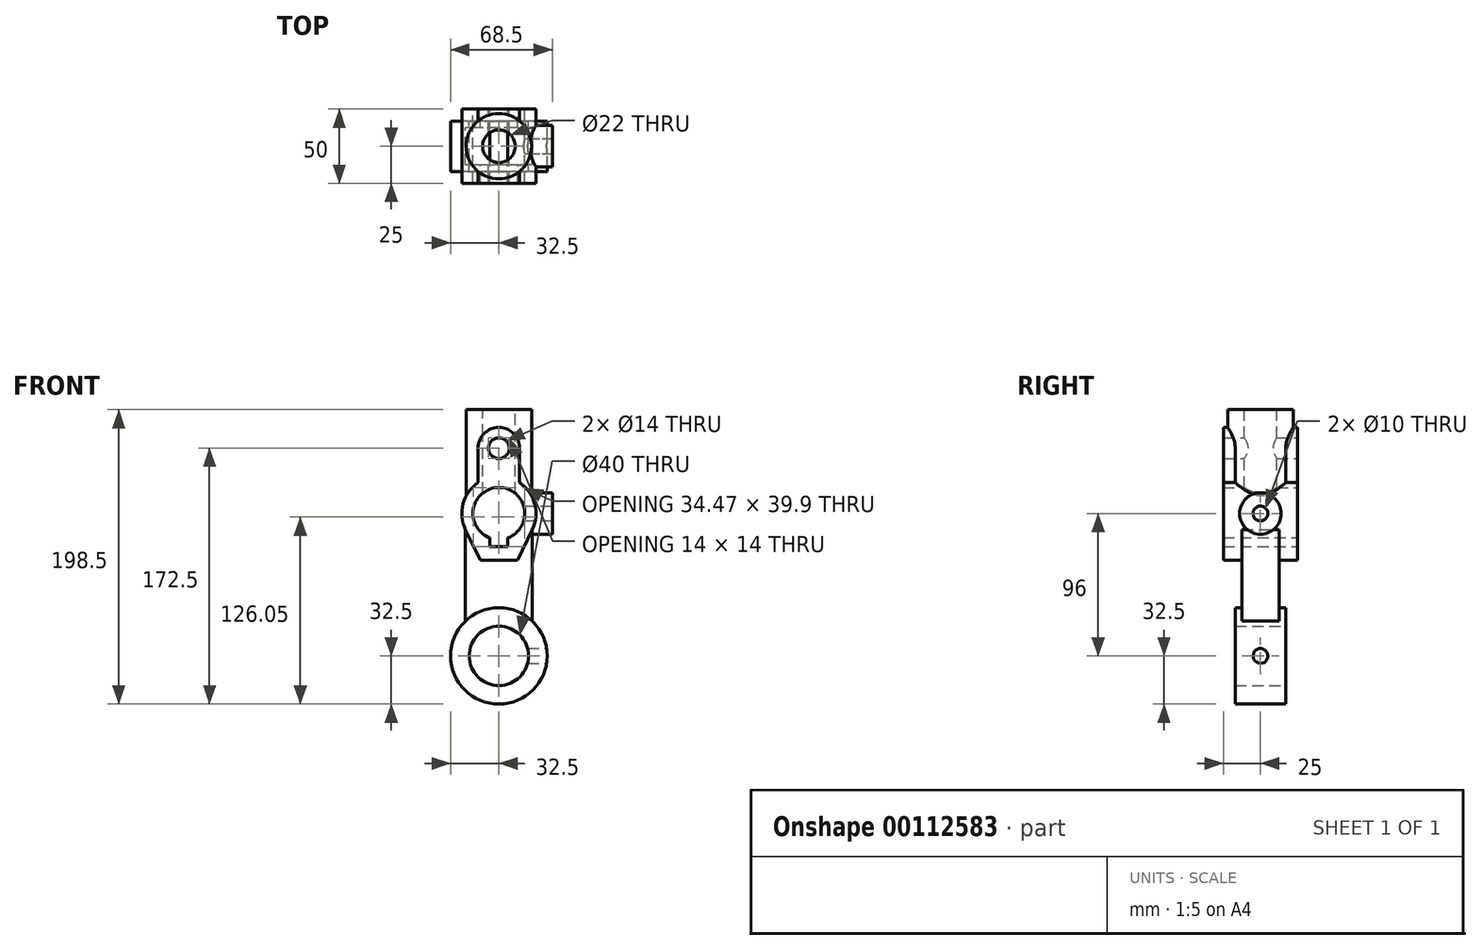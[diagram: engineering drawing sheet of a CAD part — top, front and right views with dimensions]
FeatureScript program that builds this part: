
annotation { "Feature Type Name" : "Feature", "Feature Type Description" : "" }
export const myFeature = defineFeature(function(context is Context, id is Id, definition is map)
    precondition{}
    {
        {
            var Q0;
            Q0=qCreatedBy(makeId("Front.planeOp"),FACE);
            var sketch = newSketch(context, id + "F0", { "sketchPlane" : qUnion([Q0])});
            skCircle(sketch, "E0", {"center": v(0, 0) * mm, "radius": 32.5 * mm});
            skCircle(sketch, "E1", {"center": v(0, 0) * mm, "radius": 20 * mm});
            skSolve(sketch);
        }
        {
            var Q0;
            Q0 = qSketchRegion(id + "F0", true);
            extrude(context, id + "F1", {"entities" : qUnion([Q0]), "depth" : 34 * mm, "symmetric" : true});
        }
        {
            var Q0;
            Q0=qCreatedBy(makeId("Front.planeOp"),FACE);
            var sketch = newSketch(context, id + "F2", { "sketchPlane" : qUnion([Q0])});
            skLineSegment(sketch, "E2.bottom", {"start": v(-22.5, 0) * mm, "end": v(22.5, 0) * mm});
            skLineSegment(sketch, "E2.top", {"start": v(-22.5, 96) * mm, "end": v(22.5, 96) * mm});
            skLineSegment(sketch, "E2.left", {"start": v(-22.5, 0) * mm, "end": v(-22.5, 96) * mm});
            skLineSegment(sketch, "E2.right", {"start": v(22.5, 0) * mm, "end": v(22.5, 96) * mm});
            skLineSegment(sketch, "E3", {"start": v(0, 64.95) * mm, "end": v(-22.5, 64.95) * mm, "construction": true});
            skLineSegment(sketch, "E4", {"start": v(0, 56.14) * mm, "end": v(22.5, 56.14) * mm, "construction": true});
            skSolve(sketch);
        }
        {
            var Q0;
            Q0 = qSketchRegion(id + "F2", true);
            extrude(context, id + "F3", {"entities" : qUnion([Q0]), "operationType" : NewBodyOperationType.ADD, "depth" : 25 * mm, "symmetric" : true});
        }
        {
            var Q0;
            {var subQ0=sQuery(id+"F2.wireOp",EDGE,"E2.bottom");Q0=makeQuery(id+"F3.boolean.opBoolean","SPLIT",FACE,{"disambiguationData":[TD([makeQuery(id+"F1.opExtrude","SWEPT_FACE",FACE,{"disambiguationData":[OSD([sQuery(id+"F0.wireOp",EDGE,"E1")])]})])],"derivedFrom":makeQuery(id+"F3.opExtrude","CAP_FACE",FACE,{"disambiguationData":[OSD([subQ0,sQuery(id+"F2.wireOp",EDGE,"E2.top"),sQuery(id+"F2.wireOp",EDGE,"E2.left"),sQuery(id+"F2.wireOp",EDGE,"E2.right")])],"isStart":false})});}
            extrude(context, id + "F4", {"entities" : qUnion([Q0]), "operationType" : NewBodyOperationType.REMOVE, "endBound" : BoundingType.THROUGH_ALL, "oppositeDirection" : true, "depth" : 25 * mm});
        }
        {
            var Q0;
            Q0=qCreatedBy(makeId("Front.planeOp"),FACE);
            var sketch = newSketch(context, id + "F5", { "sketchPlane" : qUnion([Q0])});
            skCircle(sketch, "E5", {"center": v(0, 140) * mm, "radius": 7 * mm});
            skArc(sketch, "E6", {"start": v(6, 79.56) * mm, "mid": v(0, 113.5) * mm, "end": v(-6, 79.56) * mm});
            skLineSegment(sketch, "E7", {"start": v(-6, 79.56) * mm, "end": v(-6, 73.6) * mm});
            skLineSegment(sketch, "E8", {"start": v(6, 79.56) * mm, "end": v(6, 73.6) * mm});
            skLineSegment(sketch, "E9", {"start": v(6, 73.6) * mm, "end": v(-6, 73.6) * mm});
            skArc(sketch, "E10", {"start": v(-14, 140) * mm, "mid": v(0, 154) * mm, "end": v(14, 140) * mm});
            skLineSegment(sketch, "E11", {"start": v(-14, 140) * mm, "end": v(-14, 116.71) * mm});
            skLineSegment(sketch, "E12", {"start": v(14, 140) * mm, "end": v(14, 116.71) * mm});
            skArc(sketch, "E13", {"start": v(-14, 116.71) * mm, "mid": v(-24.14, 102.5) * mm, "end": v(-22.5, 85.1) * mm});
            skLineSegment(sketch, "E14.0", {"start": v(-22.5, 0) * mm, "end": v(-22.5, 85.1) * mm});
            skLineSegment(sketch, "E15", {"start": v(-22.5, 85.1) * mm, "end": v(-22.5, 96) * mm});
            skLineSegment(sketch, "E16.0", {"start": v(22.5, 0) * mm, "end": v(22.5, 96) * mm});
            skArc(sketch, "E17", {"start": v(22.5, 85.1) * mm, "mid": v(24.14, 102.5) * mm, "end": v(14, 116.71) * mm});
            skLineSegment(sketch, "E18", {"start": v(-12.5, 64.46) * mm, "end": v(12.5, 64.46) * mm});
            skLineSegment(sketch, "E19", {"start": v(-22.5, 85.1) * mm, "end": v(-12.5, 64.46) * mm});
            skLineSegment(sketch, "E20", {"start": v(22.5, 85.1) * mm, "end": v(12.5, 64.46) * mm});
            skSolve(sketch);
        }
        {
            var Q0;
            Q0=makeQuery(id+"F5.imprint","IMPRINT",FACE,{"disambiguationData":[TD([[makeQuery(id+"F5.imprint","IMPRINT",EDGE,{"derivedFrom":sQuery(id+"F5.wireOp",EDGE,"E5")}),-1.0]])]});
            extrude(context, id + "F6", {"entities" : qUnion([Q0]), "operationType" : NewBodyOperationType.ADD, "depth" : 50 * mm, "symmetric" : true});
        }
        {
            var Q0;
            {var subQ0=sQuery(id+"F2.wireOp",EDGE,"E2.top");var subQ1=makeQuery(id+"F3.opExtrude","SWEPT_FACE",FACE,{"disambiguationData":[OSD([subQ0])]});var subQ2=sQuery(id+"F2.wireOp",EDGE,"E2.left");var subQ3=sQuery(id+"F2.wireOp",EDGE,"E2.right");Q0=makeQuery(id+"F6.boolean.opBoolean","SPLIT",FACE,{"disambiguationData":[TD([subQ1])],"derivedFrom":makeQuery(id+"F3.boolean.opBoolean","SPLIT",FACE,{"disambiguationData":[TD([makeQuery(id+"F1.opExtrude","SWEPT_FACE",FACE,{"disambiguationData":[OSD([sQuery(id+"F0.wireOp",EDGE,"E0")])]})])],"derivedFrom":makeQuery(id+"F3.opExtrude","CAP_FACE",FACE,{"disambiguationData":[OSD([sQuery(id+"F2.wireOp",EDGE,"E2.bottom"),subQ0,subQ2,subQ3])],"isStart":false})})});}
            extrude(context, id + "F7", {"entities" : qUnion([Q0]), "operationType" : NewBodyOperationType.REMOVE, "endBound" : BoundingType.THROUGH_ALL, "oppositeDirection" : true, "depth" : 25 * mm});
        }
        {
            var Q0;
            Q0=qCreatedBy(makeId("Top.planeOp"),FACE);
            cPlane(context, id + "F8", {"entities" : qUnion([Q0]), "cplaneType" : CPlaneType.OFFSET, "offset" : 166 * mm, "width" : 150 * mm, "height" : 150 * mm});
        }
        {
            var Q0;
            Q0=qCreatedBy(id+"F8.planeOp",FACE);
            var sketch = newSketch(context, id + "F9", { "sketchPlane" : qUnion([Q0])});
            skCircle(sketch, "E21", {"center": v(0, 0) * mm, "radius": 22 * mm});
            skSolve(sketch);
        }
        {
            var Q0;
            Q0 = qSketchRegion(id + "F9", true);
            extrude(context, id + "F10", {"entities" : qUnion([Q0]), "operationType" : NewBodyOperationType.ADD, "endBound" : BoundingType.UP_TO_NEXT, "oppositeDirection" : true, "depth" : 25 * mm});
        }
        {
            var Q0;
            Q0=makeQuery(id+"F10.opExtrude","CAP_FACE",FACE,{"disambiguationData":[OSD([sQuery(id+"F9.wireOp",EDGE,"E21")])],"isStart":true});
            var sketch = newSketch(context, id + "F11", { "sketchPlane" : qUnion([Q0])});
            skCircle(sketch, "E22", {"center": v(0, 0) * mm, "radius": 11 * mm});
            skSolve(sketch);
        }
        {
            var Q0;
            Q0 = qSketchRegion(id + "F11", true);
            extrude(context, id + "F12", {"entities" : qUnion([Q0]), "operationType" : NewBodyOperationType.REMOVE, "oppositeDirection" : true, "depth" : 70 * mm});
        }
        {
            var Q0;
            Q0=qCreatedBy(makeId("Right.planeOp"),FACE);
            cPlane(context, id + "F13", {"entities" : qUnion([Q0]), "cplaneType" : CPlaneType.OFFSET, "offset" : 36 * mm, "width" : 150 * mm, "height" : 150 * mm});
        }
        {
            var Q0;
            Q0=qCreatedBy(id+"F13.planeOp",FACE);
            var sketch = newSketch(context, id + "F14", { "sketchPlane" : qUnion([Q0])});
            skCircle(sketch, "E23", {"center": v(0, 96) * mm, "radius": 14 * mm});
            skSolve(sketch);
        }
        {
            var Q0;
            Q0=makeQuery(id+"F14.imprint","IMPRINT",FACE,{"disambiguationData":[TD([[makeQuery(id+"F14.imprint","IMPRINT",EDGE,{"derivedFrom":sQuery(id+"F14.wireOp",EDGE,"E23")}),1.0]])]});
            extrude(context, id + "F15", {"entities" : qUnion([Q0]), "operationType" : NewBodyOperationType.ADD, "endBound" : BoundingType.UP_TO_NEXT, "oppositeDirection" : true, "depth" : 25 * mm});
        }
        {
            var Q0;
            Q0=qCreatedBy(id+"F13.planeOp",FACE);
            var sketch = newSketch(context, id + "F16", { "sketchPlane" : qUnion([Q0])});
            skCircle(sketch, "E24", {"center": v(0, 96) * mm, "radius": 5 * mm});
            skSolve(sketch);
        }
        {
            var Q0;
            Q0 = qSketchRegion(id + "F16", true);
            extrude(context, id + "F17", {"entities" : qUnion([Q0]), "operationType" : NewBodyOperationType.REMOVE, "endBound" : BoundingType.UP_TO_NEXT, "oppositeDirection" : true, "depth" : 25 * mm});
        }
        {
            var Q0;
            Q0=qCreatedBy(id+"F13.planeOp",FACE);
            var sketch = newSketch(context, id + "F18", { "sketchPlane" : qUnion([Q0])});
            skCircle(sketch, "E25", {"center": v(0, 0) * mm, "radius": 5 * mm});
            skSolve(sketch);
        }
        {
            var Q0;
            Q0 = qSketchRegion(id + "F18", true);
            extrude(context, id + "F19", {"entities" : qUnion([Q0]), "operationType" : NewBodyOperationType.REMOVE, "oppositeDirection" : true, "depth" : 25 * mm});
        }
    });
